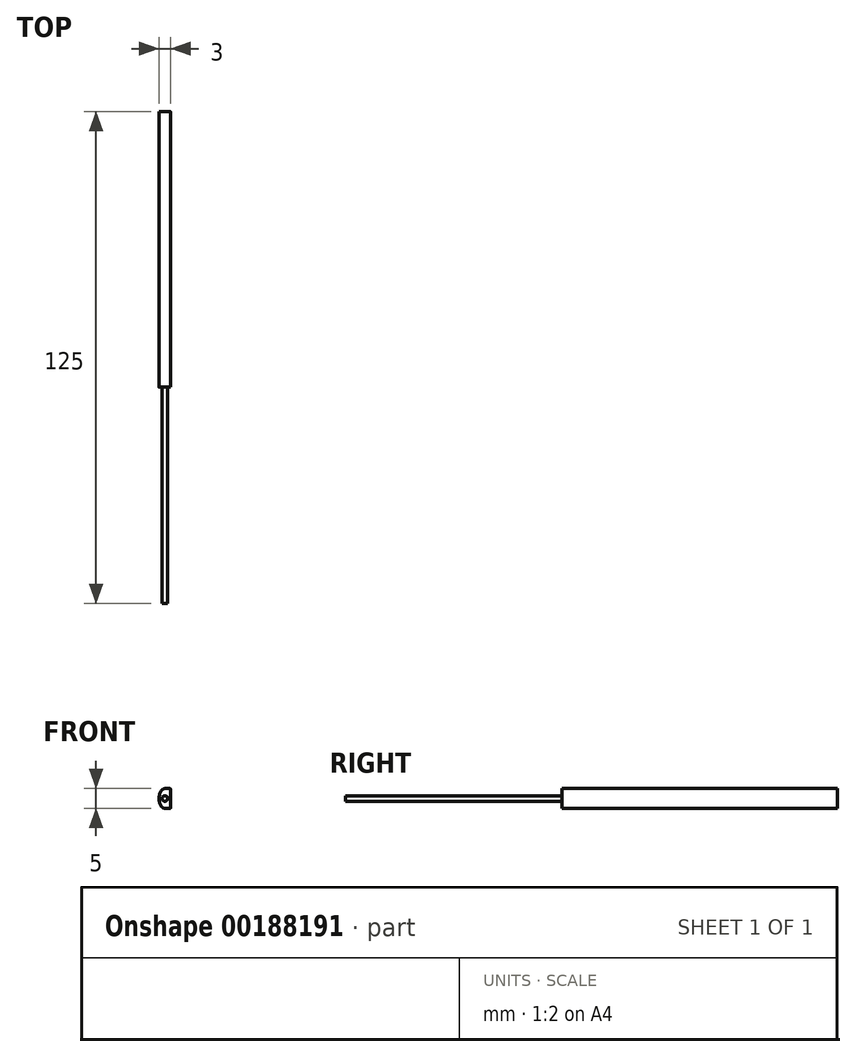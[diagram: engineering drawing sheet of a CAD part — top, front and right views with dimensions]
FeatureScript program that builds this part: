
annotation { "Feature Type Name" : "Feature", "Feature Type Description" : "" }
export const myFeature = defineFeature(function(context is Context, id is Id, definition is map)
    precondition{}
    {
        {
            var Q0;
            Q0=qCreatedBy(makeId("Front.planeOp"),FACE);
            var sketch = newSketch(context, id + "F0", { "sketchPlane" : qUnion([Q0])});
            skCircle(sketch, "E0", {"center": v(0, 0) * mm, "radius": 0.7 * mm});
            skSolve(sketch);
        }
        {
            var Q0;
            Q0 = qSketchRegion(id + "F0", true);
            extrude(context, id + "F1", {"entities" : qUnion([Q0]), "depth" : 55 * mm});
        }
        {
            var Q0;
            Q0=qCreatedBy(makeId("Front.planeOp"),FACE);
            var sketch = newSketch(context, id + "F2", { "sketchPlane" : qUnion([Q0])});
            skLineSegment(sketch, "E1", {"start": v(1.5, 2.5) * mm, "end": v(1.5, -2.5) * mm});
            skPoint(sketch, "E2", {"position": v(1.5, 0) * mm});
            skLineSegment(sketch, "E3", {"start": v(1.5, 2.5) * mm, "end": v(0, 2.5) * mm});
            skLineSegment(sketch, "E4", {"start": v(1.5, -2.5) * mm, "end": v(0, -2.5) * mm});
            skArc(sketch, "E5", {"start": v(-0.8, 2.1) * mm, "mid": v(-1.5, 0) * mm, "end": v(-0.8, -2.1) * mm});
            skPoint(sketch, "E6.visualSharp", {"position": v(-0.45, 2.5) * mm});
            skArc(sketch, "E6.filletArc", {"start": v(0, 2.5) * mm, "mid": v(-0.45, 2.4) * mm, "end": v(-0.8, 2.1) * mm});
            skPoint(sketch, "E7.visualSharp", {"position": v(-0.45, -2.5) * mm});
            skArc(sketch, "E7.filletArc", {"start": v(-0.8, -2.1) * mm, "mid": v(-0.45, -2.4) * mm, "end": v(0, -2.5) * mm});
            skSolve(sketch);
        }
        {
            var Q0;
            Q0 = qSketchRegion(id + "F2", true);
            extrude(context, id + "F3", {"entities" : qUnion([Q0]), "operationType" : NewBodyOperationType.ADD, "oppositeDirection" : true, "depth" : 70 * mm});
        }
        {
            var Q0;
            Q0=makeQuery(id+"F3.opExtrude","SWEPT_EDGE",EDGE,{"disambiguationData":[OSD([sQuery(id+"F2.wireOp",EDGE,"E1"),sQuery(id+"F2.wireOp",EDGE,"E3")])]});
            var Q1;
            Q1=makeQuery(id+"F3.opExtrude","SWEPT_EDGE",EDGE,{"disambiguationData":[OSD([sQuery(id+"F2.wireOp",EDGE,"E1"),sQuery(id+"F2.wireOp",EDGE,"E4")])]});
            fillet(context, id + "F4", {"entities" : qUnion([Q0, Q1]), "radius" : 0.2 * mm, "tangentPropagation" : true, "allowEdgeOverflow" : false});
        }
    });
